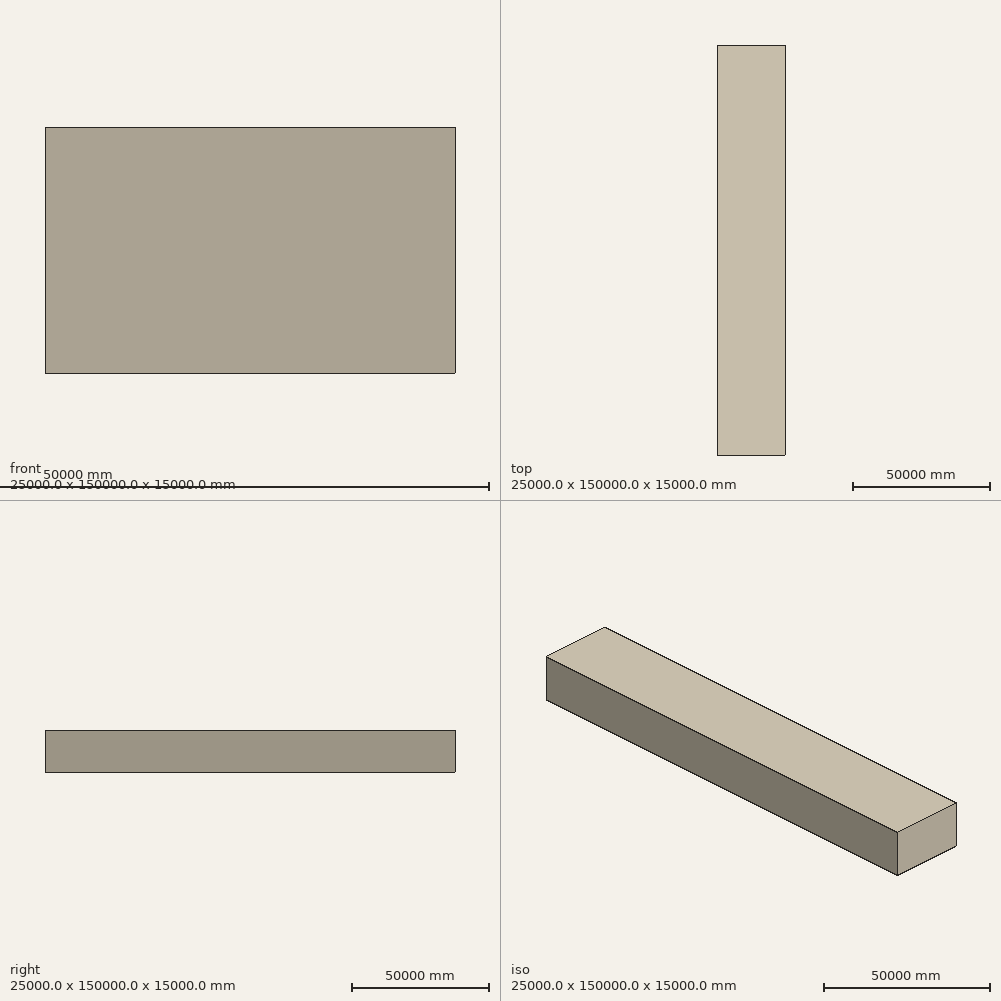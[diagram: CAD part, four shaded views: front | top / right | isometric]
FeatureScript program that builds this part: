
annotation { "Feature Type Name" : "Feature", "Feature Type Description" : "" }
export const myFeature = defineFeature(function(context is Context, id is Id, definition is map)
    precondition{}
    {
        {
            var Q0;
            Q0=qCreatedBy(makeId("Right.planeOp"),FACE);
            var sketch = newSketch(context, id + "F0", { "sketchPlane" : qUnion([Q0])});
            skLineSegment(sketch, "E0", {"start": v(0, 0) * mm, "end": v(150000, 0) * mm});
            skLineSegment(sketch, "E1", {"start": v(0, 0) * mm, "end": v(0, 15000) * mm});
            skLineSegment(sketch, "E2", {"start": v(0, 15000) * mm, "end": v(150000, 15000) * mm});
            skLineSegment(sketch, "E3", {"start": v(150000, 15000) * mm, "end": v(150000, 0) * mm});
            skSolve(sketch);
        }
        {
            var Q0;
            Q0=makeQuery(id+"F0.imprint","IMPRINT",FACE,{"disambiguationData":[TD([[makeQuery(id+"F0.imprint","IMPRINT",EDGE,{"derivedFrom":sQuery(id+"F0.wireOp",EDGE,"E0")}),1.0]])]});
            extrude(context, id + "F1", {"entities" : qUnion([Q0]), "depth" : 25000 * mm, "offsetDistance" : 25 * mm});
        }
    });
